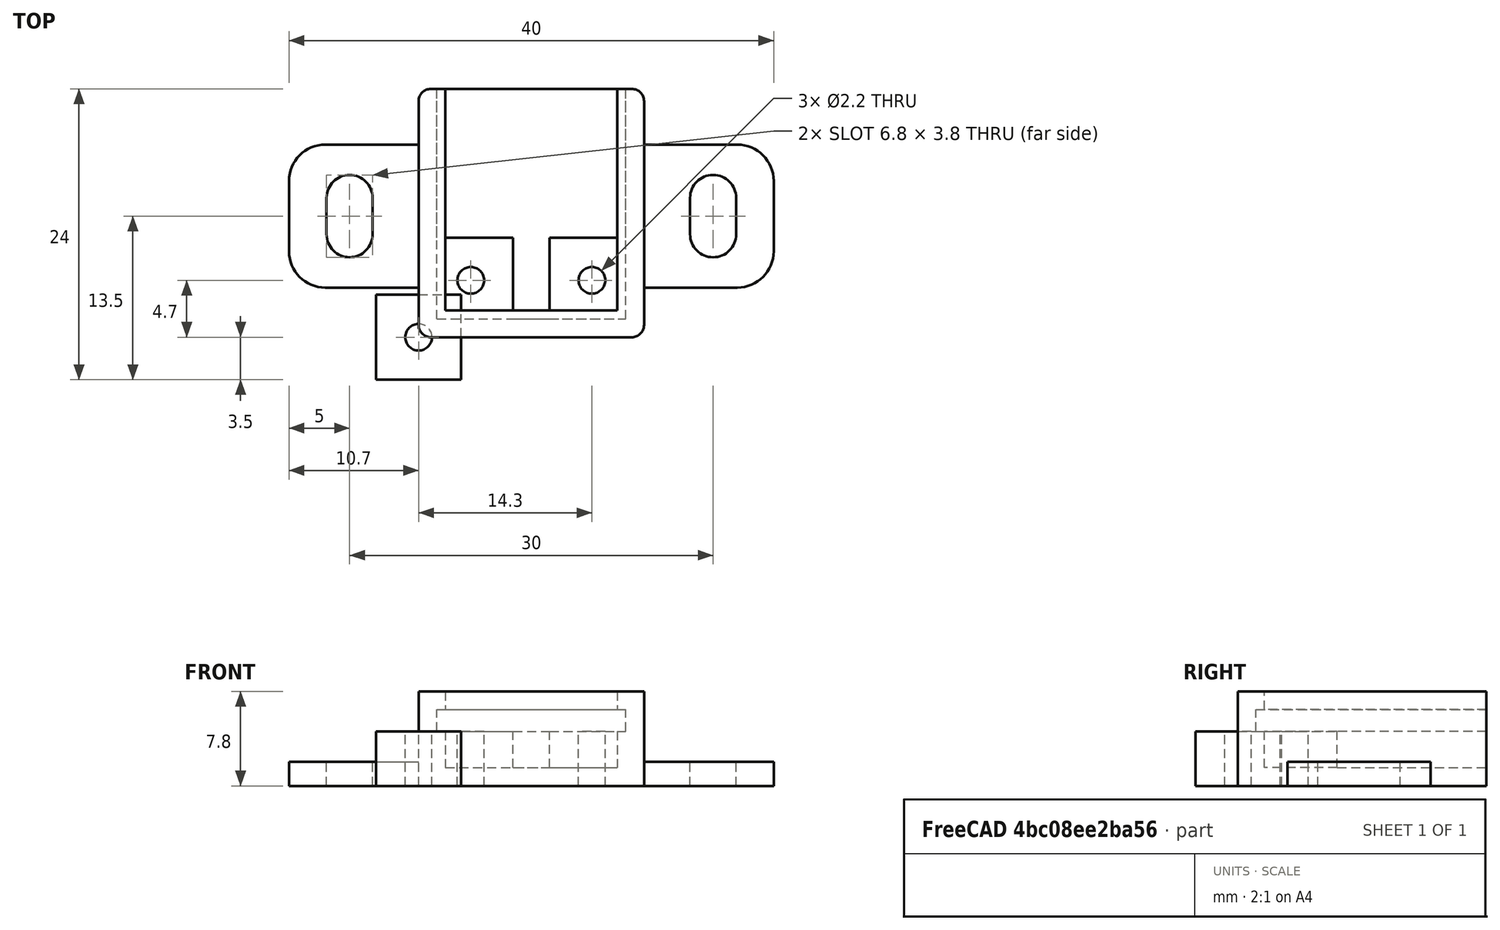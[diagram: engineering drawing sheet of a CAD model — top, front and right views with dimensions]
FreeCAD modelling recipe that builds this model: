
FCSTD DOCUMENT  (FreeCAD 0.19R23578 (Git))
Label: ir_sensor_qc
License: FreeArt
LicenseURL: http://artlibre.org/licence/lal
objects: Part::Box×4, Part::MultiFuse×3, Part::Cut×3, Part::FeaturePython×2, Spreadsheet::Sheet×1, Part::Fillet×1, Part::Cylinder×1, Part::Feature×1, App::Part×1
note: 13 computed .brp shape members not serialized (recipe doc carries the construction recipe); baked Part::Feature solids carry a one-line shape summary decoded from their .brp

FEATURE [Spreadsheet::Sheet] Spreadsheet  label="p"
  cells = A1=pcb_x; B1(pcb_x)=15.6; A2=pcb_y; B2(pcb_y)=19; A3=pcb_z; B3(pcb_z)=1.8; A4=pcb_under; B4(pcb_under)=3; A5=side_wall; B5(side_wall)=1.5; A6=pcb_side_lane; B6(pcb_side_lane)=0.7; A7=bottom_wall; B7(bottom_wall)=1.5; A8=pcb_above; B8(pcb_above)=1.5; A9=hole_dist_x; B9(hole_dist_x)=10; A10=hole_r; B10(hole_r)=1.1; A11=hole_off_y; B11(hole_off_y)=3.2; A12=hole_stand_size; B12(hole_stand_size)=7
FEATURE [Part::Box] Box  label="external cube"
  AttacherType = Attacher::AttachEngine3D
  Height = 7.8
  Length = 18.6
  Width = 20.5
  expr: Height = <<p>>.bottom_wall + <<p>>.pcb_under + <<p>>.pcb_z + <<p>>.pcb_above
  expr: Width = <<p>>.pcb_y + <<p>>.side_wall
  expr: Length = <<p>>.pcb_x + 2 * <<p>>.side_wall
FEATURE [Part::Box] Box006  label="internal cube"
  AttacherType = Attacher::AttachEngine3D
  Height = 6.3
  Length = 14.2
  Placement = pos=(2.2,2.2,1.5) rot=(0,0,1;0rad)
  Width = 19.1
  expr: .Placement.Base.y = <<p>>.side_wall + <<p>>.pcb_side_lane
  expr: .Placement.Base.x = <<p>>.side_wall + <<p>>.pcb_side_lane
  expr: .Placement.Base.z = <<p>>.bottom_wall
  expr: Height = <<p>>.pcb_under + <<p>>.pcb_z + <<p>>.pcb_above
  expr: Width = <<p>>.pcb_y - 2 * <<p>>.pcb_side_lane + <<p>>.side_wall
  expr: Length = <<p>>.pcb_x - 2 * <<p>>.pcb_side_lane
FEATURE [Part::Box] Box007  label="pcb extract cube"
  AttacherType = Attacher::AttachEngine3D
  Height = 1.8
  Length = 15.6
  Placement = pos=(1.5,1.5,4.5) rot=(0,0,1;0rad)
  Width = 19
  expr: .Placement.Base.y = <<p>>.side_wall
  expr: .Placement.Base.x = <<p>>.side_wall
  expr: Length = <<p>>.pcb_x
  expr: Width = <<p>>.pcb_y
  expr: .Placement.Base.z = <<p>>.bottom_wall + <<p>>.pcb_under
  expr: Height = <<p>>.pcb_z
FEATURE [Part::MultiFuse] Fusion  label="extract fusion"
  Shapes = -> [Box006,Box007]
FEATURE [Part::Fillet] Fillet  label="external fillet"
  Base = -> Box
  Edges = 4 edges r=1: [Edge1,Edge3,Edge5,Edge7]
FEATURE [Part::Cylinder] Cylinder  label="hole"
  Angle = 360
  AttacherType = Attacher::AttachEngine3D
  Height = 10
  Radius = 1.1
  expr: Radius = <<p>>.hole_r
FEATURE [Part::Box] Box008  label="stand"
  AttacherType = Attacher::AttachEngine3D
  Height = 4.5
  Length = 7
  Placement = pos=(-3.5,-3.5,0) rot=(0,0,1;0rad)
  Width = 7
  expr: Height = <<p>>.pcb_under + <<p>>.bottom_wall
  expr: Length = <<p>>.hole_stand_size
  expr: Width = <<p>>.hole_stand_size
  expr: .Placement.Base.x = -<<p>>.hole_stand_size / 2
  expr: .Placement.Base.y = -<<p>>.hole_stand_size / 2
FEATURE [Part::FeaturePython] Array  label="hole array"  # Draft array (typed FeaturePython)
  Angle = 360
  ArrayType = 0
  Axis = (0,0,1)
  Base = -> Box008
  Center = (0,0,0)
  Count = 2
  ExpandArray = false
  Fuse = false
  IntervalAxis = (0,0,0)
  IntervalX = (10,0,0)
  IntervalY = (0,1,0)
  IntervalZ = (0,0,100)
  NumberCircles = 3
  NumberPolar = 5
  NumberX = 2
  NumberY = 1
  NumberZ = 1
  Placement = pos=(4.3,4.7,0) rot=(0,0,1;0rad)
  PlacementList = 2 placements: [(-3.5,-3.5,0),(6.5,-3.5,0)]
  RadialDistance = 50
  ScaleList = (2) [(1,1,1),(1,1,1)]
  Symmetry = 1
  TangentialDistance = 25
  expr: .Placement.Base.y = Spreadsheet.hole_off_y + <<p>>.side_wall
  expr: .Placement.Base.x = (2 * <<p>>.side_wall + <<p>>.pcb_x - Spreadsheet.hole_dist_x) / 2
  expr: .IntervalX.x = Spreadsheet.hole_dist_x
FEATURE [Part::Cut] Cut003002  label="stand hole cut"
  Base = -> Box008
  Tool = -> Cylinder
FEATURE [Part::FeaturePython] Array001  label="hole array001"  # Draft array (typed FeaturePython)
  Angle = 360
  ArrayType = 0
  Axis = (0,0,1)
  Base = -> Cylinder
  Center = (0,0,0)
  Count = 2
  ExpandArray = false
  Fuse = false
  IntervalAxis = (0,0,0)
  IntervalX = (10,0,0)
  IntervalY = (0,1,0)
  IntervalZ = (0,0,100)
  NumberCircles = 3
  NumberPolar = 5
  NumberX = 2
  NumberY = 1
  NumberZ = 1
  Placement = pos=(4.3,4.7,0) rot=(0,0,1;0rad)
  PlacementList = 2 placements: [(0,0,0),(10,0,0)]
  RadialDistance = 50
  ScaleList = (2) [(1,1,1),(1,1,1)]
  Symmetry = 1
  TangentialDistance = 25
  expr: .IntervalX.x = Spreadsheet.hole_dist_x
  expr: .Placement.Base.x = (2 * <<p>>.side_wall + <<p>>.pcb_x - Spreadsheet.hole_dist_x) / 2
  expr: .Placement.Base.y = Spreadsheet.hole_off_y + <<p>>.side_wall
FEATURE [Part::Feature] Cut003001  label="attach plane x dir001"
  Placement = pos=(-10.7,4.1,0) rot=(0,0,1;0rad)
  shape: bbox 40 x 11.8 x 2 mm, 18 faces (baked)
FEATURE [Part::MultiFuse] Fusion001  label="body fusion"
  Shapes = -> [Fillet,Cut003001]
FEATURE [Part::Cut] Cut  label="body cut003"
  Base = -> Fusion001
  Tool = -> Fusion
FEATURE [Part::MultiFuse] Fusion002  label="body fusion003"
  Shapes = -> [Array,Cut]
FEATURE [Part::Cut] Cut003003  label="body cut"
  Base = -> Fusion002
  Tool = -> Array001
FEATURE [App::Part] Part  label="box part"
  Group = -> [Box,Fillet,Fusion001,Fusion,Box007,Box006,Cut,Cylinder,Box008,Cut003002,Array,Fusion002,Array001,Cut003003]
  Origin = -> Origin
